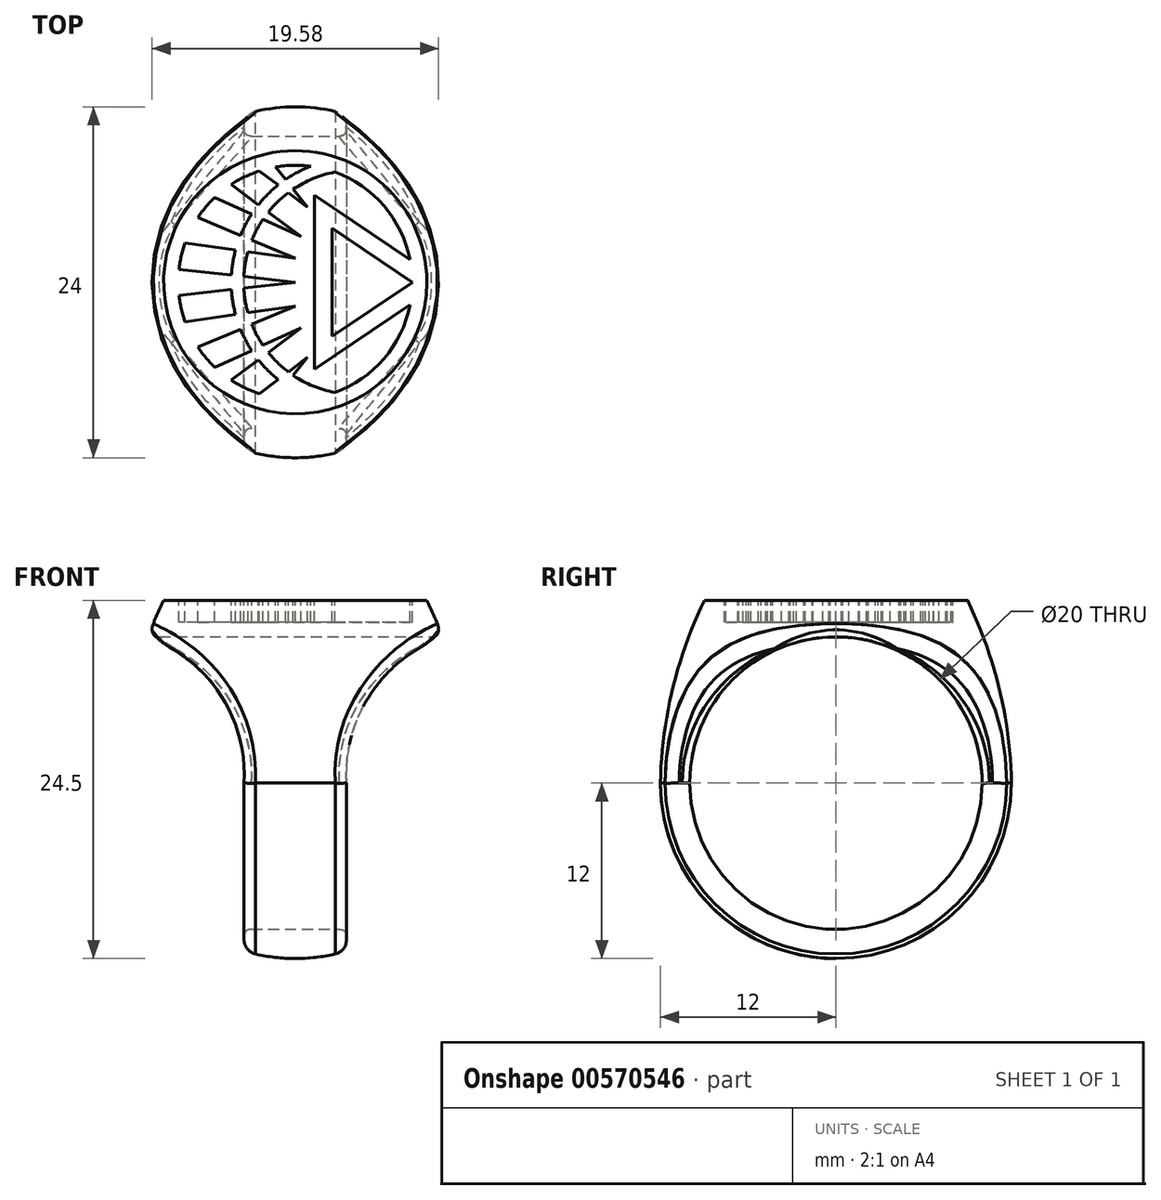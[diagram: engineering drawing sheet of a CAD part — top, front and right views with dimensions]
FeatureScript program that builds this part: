
annotation { "Feature Type Name" : "Feature", "Feature Type Description" : "" }
export const myFeature = defineFeature(function(context is Context, id is Id, definition is map)
    precondition{}
    {
        {
            var Q0;
            Q0=qCreatedBy(makeId("Right.planeOp"),FACE);
            var sketch = newSketch(context, id + "F0", { "sketchPlane" : qUnion([Q0])});
            skLineSegment(sketch, "E0", {"start": v(0, 0) * mm, "end": v(0, -24.5) * mm});
            skLineSegment(sketch, "E1", {"start": v(0, 0) * mm, "end": v(-9, 0) * mm});
            skArc(sketch, "E2", {"start": v(-12, -12.5) * mm, "mid": v(-8.49, -20.99) * mm, "end": v(0, -24.5) * mm});
            skLineSegment(sketch, "E3", {"start": v(0, -12.5) * mm, "end": v(-12, -12.5) * mm, "construction": true});
            skArc(sketch, "E4", {"start": v(-9, 0) * mm, "mid": v(-11.18, -6.09) * mm, "end": v(-12, -12.5) * mm});
            skSolve(sketch);
        }
        {
            var Q0;
            Q0=makeQuery(id+"F0.imprint","IMPRINT",FACE,{"disambiguationData":[TD([[makeQuery(id+"F0.imprint","IMPRINT",EDGE,{"derivedFrom":sQuery(id+"F0.wireOp",EDGE,"E0")}),-1.0]])]});
            var Q1;
            Q1=sQuery(id+"F0.wireOp",EDGE,"E0");
            revolve(context, id + "F1", {"entities" : qUnion([Q0]), "axis" : qUnion([Q1]), "revolveType" : RevolveType.FULL});
        }
        {
            var Q0;
            Q0=qCreatedBy(makeId("Right.planeOp"),FACE);
            var sketch = newSketch(context, id + "F2", { "sketchPlane" : qUnion([Q0])});
            skCircle(sketch, "E5", {"center": v(0, -12.5) * mm, "radius": 10 * mm});
            skSolve(sketch);
        }
        {
            var Q0;
            Q0=qSketchRegion(id+"F2",true);
            extrude(context, id + "F3", {"entities" : qUnion([Q0]), "operationType" : NewBodyOperationType.REMOVE, "oppositeDirection" : true, "depth" : 25 * mm, "offsetDistance" : 25 * mm, "symmetric" : true});
        }
        {
            var Q0;
            Q0=qCreatedBy(makeId("Front.planeOp"),FACE);
            var sketch = newSketch(context, id + "F4", { "sketchPlane" : qUnion([Q0])});
            skLineSegment(sketch, "E6", {"start": v(3.5, -26.5) * mm, "end": v(3.5, -12.5) * mm});
            skArc(sketch, "E7", {"start": v(10.15, -2.5) * mm, "mid": v(5.16, -6.39) * mm, "end": v(3.5, -12.5) * mm});
            skLineSegment(sketch, "E8", {"start": v(10.15, -2.5) * mm, "end": v(11.65, -2.5) * mm});
            skLineSegment(sketch, "E9", {"start": v(11.65, -2.5) * mm, "end": v(11.65, -26.5) * mm});
            skLineSegment(sketch, "E10", {"start": v(11.65, -26.5) * mm, "end": v(3.5, -26.5) * mm});
            skPoint(sketch, "E11.start.orphan", {"position": v(0, -24.5) * mm});
            skLineSegment(sketch, "E12", {"start": v(0, 0) * mm, "end": v(0, -24.5) * mm, "construction": true});
            skLineSegment(sketch, "E13.MirrorCS", {"start": v(-3.5, -26.5) * mm, "end": v(-3.5, -12.5) * mm});
            skArc(sketch, "E14.MirrorCS", {"start": v(-10.15, -2.5) * mm, "mid": v(-5.16, -6.39) * mm, "end": v(-3.5, -12.5) * mm});
            skLineSegment(sketch, "E15.MirrorCS", {"start": v(-11.65, -2.5) * mm, "end": v(-11.65, -26.5) * mm});
            skLineSegment(sketch, "E16.MirrorCS", {"start": v(-11.65, -26.5) * mm, "end": v(-3.5, -26.5) * mm});
            skLineSegment(sketch, "E17.MirrorCS", {"start": v(-10.15, -2.5) * mm, "end": v(-11.65, -2.5) * mm});
            skSolve(sketch);
        }
        {
            var Q0;
            Q0=qSketchRegion(id+"F4",true);
            extrude(context, id + "F5", {"entities" : qUnion([Q0]), "operationType" : NewBodyOperationType.REMOVE, "depth" : 25 * mm, "offsetDistance" : 25 * mm, "symmetric" : true});
        }
        {
            var Q0;
            Q0=makeQuery(id+"F1.opRevolve","SWEPT_FACE",FACE,{"disambiguationData":[OSD([sQuery(id+"F0.wireOp",EDGE,"E1")])]});
            var sketch = newSketch(context, id + "F6", { "sketchPlane" : qUnion([Q0])});
            skLineSegment(sketch, "E18", {"start": v(-8, 0) * mm, "end": v(8, 0) * mm, "construction": true});
            skArc(sketch, "E19", {"start": v(1.04, 7.93) * mm, "mid": v(-0.15, 8) * mm, "end": v(-1.34, 7.89) * mm});
            skLineSegment(sketch, "E20", {"start": v(7.85, 1.55) * mm, "end": v(1.3, 5.96) * mm});
            skLineSegment(sketch, "E21", {"start": v(1.3, 5.96) * mm, "end": v(1.3, 0) * mm});
            skLineSegment(sketch, "E22", {"start": v(8, 0) * mm, "end": v(2.5, 3.7) * mm});
            skLineSegment(sketch, "E23", {"start": v(2.5, 3.7) * mm, "end": v(2.5, 0) * mm});
            skLineSegment(sketch, "E24", {"start": v(0, 0) * mm, "end": v(-7.95, 0.89) * mm});
            skLineSegment(sketch, "E25", {"start": v(0.85, 5.13) * mm, "end": v(-0.14, 6.37) * mm});
            skLineSegment(sketch, "E26", {"start": v(0.85, 5.13) * mm, "end": v(-0.48, 6.13) * mm});
            skLineSegment(sketch, "E27", {"start": v(0.4, 3.12) * mm, "end": v(-1.85, 4.8) * mm});
            skLineSegment(sketch, "E28", {"start": v(0.4, 3.12) * mm, "end": v(-2.2, 4.3) * mm});
            skLineSegment(sketch, "E29", {"start": v(0, 1.63) * mm, "end": v(-2.97, 2.88) * mm});
            skLineSegment(sketch, "E30", {"start": v(0, 1.63) * mm, "end": v(-3.24, 2.09) * mm});
            skArc(sketch, "E31", {"start": v(2.7, 7.53) * mm, "mid": v(1.22, 7.1) * mm, "end": v(-0.14, 6.37) * mm});
            skArc(sketch, "E32", {"start": v(1.04, 7.93) * mm, "mid": v(0.16, 7.53) * mm, "end": v(-0.66, 7.03) * mm});
            skLineSegment(sketch, "E33.MirrorCS", {"start": v(8, 0) * mm, "end": v(2.5, -3.7) * mm});
            skLineSegment(sketch, "E34.MirrorCS", {"start": v(7.85, -1.55) * mm, "end": v(1.3, -5.96) * mm});
            skLineSegment(sketch, "E35.MirrorCS", {"start": v(2.5, -3.7) * mm, "end": v(2.5, 0) * mm});
            skLineSegment(sketch, "E36.MirrorCS", {"start": v(1.3, -5.96) * mm, "end": v(1.3, 0) * mm});
            skLineSegment(sketch, "E37.MirrorCS", {"start": v(0, 0) * mm, "end": v(-7.95, -0.89) * mm});
            skArc(sketch, "E38.MirrorCS", {"start": v(2.7, -7.53) * mm, "mid": v(1.22, -7.1) * mm, "end": v(-0.14, -6.37) * mm});
            skArc(sketch, "E39.MirrorCS", {"start": v(1.04, -7.93) * mm, "mid": v(0.16, -7.53) * mm, "end": v(-0.66, -7.03) * mm});
            skLineSegment(sketch, "E40.MirrorCS", {"start": v(0, -1.63) * mm, "end": v(-3.24, -2.09) * mm});
            skLineSegment(sketch, "E41.MirrorCS", {"start": v(0, -1.63) * mm, "end": v(-2.97, -2.88) * mm});
            skLineSegment(sketch, "E42.MirrorCS", {"start": v(0.4, -3.12) * mm, "end": v(-2.2, -4.3) * mm});
            skLineSegment(sketch, "E43.MirrorCS", {"start": v(0.4, -3.12) * mm, "end": v(-1.85, -4.8) * mm});
            skLineSegment(sketch, "E44.MirrorCS", {"start": v(0.85, -5.13) * mm, "end": v(-0.48, -6.13) * mm});
            skLineSegment(sketch, "E45.MirrorCS", {"start": v(0.85, -5.13) * mm, "end": v(-0.14, -6.37) * mm});
            skArc(sketch, "E46.trimOffspring", {"start": v(-1.17, 6.65) * mm, "mid": v(-1.89, 6.02) * mm, "end": v(-2.53, 5.3) * mm});
            skLineSegment(sketch, "E47.trimOffspring", {"start": v(-0.66, 7.03) * mm, "end": v(-1.34, 7.89) * mm});
            skLineSegment(sketch, "E48.trimOffspring", {"start": v(-1.17, 6.65) * mm, "end": v(-2.45, 7.62) * mm});
            skArc(sketch, "E49.trimOffspring", {"start": v(-0.48, 6.13) * mm, "mid": v(-1.2, 5.5) * mm, "end": v(-1.85, 4.8) * mm});
            skArc(sketch, "E50.trimOffspring", {"start": v(7.85, 1.55) * mm, "mid": v(6.06, 5.22) * mm, "end": v(2.7, 7.53) * mm});
            skLineSegment(sketch, "E51.trimOffspring", {"start": v(-2.53, 5.3) * mm, "end": v(-4.39, 6.7) * mm});
            skArc(sketch, "E52.trimOffspring", {"start": v(-2.99, 4.66) * mm, "mid": v(-3.4, 3.95) * mm, "end": v(-3.75, 3.21) * mm});
            skArc(sketch, "E53.trimOffspring", {"start": v(-2.2, 4.3) * mm, "mid": v(-2.63, 3.61) * mm, "end": v(-2.97, 2.88) * mm});
            skLineSegment(sketch, "E54.trimOffspring", {"start": v(-2.99, 4.66) * mm, "end": v(-5.5, 5.8) * mm});
            skArc(sketch, "E55.trimOffspring", {"start": v(-2.45, 7.62) * mm, "mid": v(-3.45, 7.22) * mm, "end": v(-4.39, 6.7) * mm});
            skArc(sketch, "E56.trimOffspring", {"start": v(-5.5, 5.8) * mm, "mid": v(-6.12, 5.16) * mm, "end": v(-6.66, 4.44) * mm});
            skArc(sketch, "E57.trimOffspring", {"start": v(-3.24, 2.09) * mm, "mid": v(-3.46, 1.05) * mm, "end": v(-3.53, 0) * mm});
            skLineSegment(sketch, "E58.trimOffspring", {"start": v(-3.75, 3.21) * mm, "end": v(-6.66, 4.44) * mm});
            skArc(sketch, "E59.trimOffspring", {"start": v(-4.08, 2.2) * mm, "mid": v(-4.3, 1.11) * mm, "end": v(-4.38, 0) * mm});
            skLineSegment(sketch, "E60.trimOffspring", {"start": v(-4.08, 2.2) * mm, "end": v(-7.53, 2.7) * mm});
            skArc(sketch, "E61.trimOffspring", {"start": v(-7.53, 2.7) * mm, "mid": v(-7.8, 1.8) * mm, "end": v(-7.95, 0.89) * mm});
            skArc(sketch, "E62.trimOffspring", {"start": v(-7.95, -0.89) * mm, "mid": v(-7.8, -1.8) * mm, "end": v(-7.53, -2.7) * mm});
            skArc(sketch, "E63.trimOffspring", {"start": v(-6.66, -4.44) * mm, "mid": v(-6.12, -5.16) * mm, "end": v(-5.5, -5.8) * mm});
            skArc(sketch, "E64.trimOffspring", {"start": v(-4.39, -6.7) * mm, "mid": v(-3.45, -7.22) * mm, "end": v(-2.45, -7.62) * mm});
            skArc(sketch, "E65.trimOffspring", {"start": v(-1.34, -7.89) * mm, "mid": v(-0.15, -8) * mm, "end": v(1.04, -7.93) * mm});
            skArc(sketch, "E66.trimOffspring", {"start": v(2.7, -7.53) * mm, "mid": v(6.06, -5.22) * mm, "end": v(7.85, -1.55) * mm});
            skLineSegment(sketch, "E67.trimOffspring", {"start": v(-0.66, -7.03) * mm, "end": v(-1.34, -7.89) * mm});
            skArc(sketch, "E68.trimOffspring", {"start": v(-1.17, -6.65) * mm, "mid": v(-1.89, -6.02) * mm, "end": v(-2.53, -5.3) * mm});
            skLineSegment(sketch, "E69.trimOffspring", {"start": v(-1.17, -6.65) * mm, "end": v(-2.45, -7.62) * mm});
            skArc(sketch, "E70.trimOffspring", {"start": v(-0.48, -6.13) * mm, "mid": v(-1.2, -5.5) * mm, "end": v(-1.85, -4.8) * mm});
            skLineSegment(sketch, "E71.trimOffspring", {"start": v(-2.53, -5.3) * mm, "end": v(-4.39, -6.7) * mm});
            skArc(sketch, "E72.trimOffspring", {"start": v(-2.2, -4.3) * mm, "mid": v(-2.63, -3.61) * mm, "end": v(-2.97, -2.88) * mm});
            skLineSegment(sketch, "E73.trimOffspring", {"start": v(-2.99, -4.66) * mm, "end": v(-5.5, -5.8) * mm});
            skArc(sketch, "E74.trimOffspring", {"start": v(-2.99, -4.66) * mm, "mid": v(-3.4, -3.95) * mm, "end": v(-3.75, -3.21) * mm});
            skLineSegment(sketch, "E75.trimOffspring", {"start": v(-3.75, -3.21) * mm, "end": v(-6.66, -4.44) * mm});
            skArc(sketch, "E76.trimOffspring", {"start": v(-3.24, -2.09) * mm, "mid": v(-3.46, -1.05) * mm, "end": v(-3.53, 0) * mm});
            skLineSegment(sketch, "E77.trimOffspring", {"start": v(-4.08, -2.2) * mm, "end": v(-7.53, -2.7) * mm});
            skArc(sketch, "E78.trimOffspring", {"start": v(-4.08, -2.2) * mm, "mid": v(-4.3, -1.11) * mm, "end": v(-4.38, 0) * mm});
            skSolve(sketch);
        }
        {
            var Q0;
            {var subQ4=sQuery(id+"F6.wireOp",EDGE,"E60.trimOffspring");Q0=makeQuery(id+"F6.imprint","IMPRINT",FACE,{"disambiguationData":[TD([[makeQuery(id+"F6.imprint","IMPRINT",EDGE,{"derivedFrom":subQ4}),1.0]])]});}
            var Q1;
            Q1=makeQuery(id+"F6.imprint","IMPRINT",FACE,{"disambiguationData":[TD([[makeQuery(id+"F6.imprint","IMPRINT",EDGE,{"derivedFrom":sQuery(id+"F6.wireOp",EDGE,"E52.trimOffspring")}),-1.0]])]});
            var Q2;
            Q2=makeQuery(id+"F6.imprint","IMPRINT",FACE,{"disambiguationData":[TD([[makeQuery(id+"F6.imprint","IMPRINT",EDGE,{"derivedFrom":sQuery(id+"F6.wireOp",EDGE,"E46.trimOffspring")}),-1.0]])]});
            var Q3;
            Q3=makeQuery(id+"F6.imprint","IMPRINT",FACE,{"disambiguationData":[TD([[makeQuery(id+"F6.imprint","IMPRINT",EDGE,{"derivedFrom":sQuery(id+"F6.wireOp",EDGE,"E19")}),1.0]])]});
            var Q4;
            Q4=makeQuery(id+"F6.imprint","IMPRINT",FACE,{"disambiguationData":[TD([[makeQuery(id+"F6.imprint","IMPRINT",EDGE,{"derivedFrom":sQuery(id+"F6.wireOp",EDGE,"E20")}),-1.0]])]});
            var Q5;
            Q5=makeQuery(id+"F6.imprint","IMPRINT",FACE,{"disambiguationData":[TD([[makeQuery(id+"F6.imprint","IMPRINT",EDGE,{"derivedFrom":sQuery(id+"F6.wireOp",EDGE,"E22")}),1.0]])]});
            var Q6;
            {var subQ0=sQuery(id+"F6.wireOp",EDGE,"E62.trimOffspring");Q6=makeQuery(id+"F6.imprint","IMPRINT",FACE,{"disambiguationData":[TD([[makeQuery(id+"F6.imprint","IMPRINT",EDGE,{"derivedFrom":subQ0}),1.0]])]});}
            var Q7;
            Q7=makeQuery(id+"F6.imprint","IMPRINT",FACE,{"disambiguationData":[TD([[makeQuery(id+"F6.imprint","IMPRINT",EDGE,{"derivedFrom":sQuery(id+"F6.wireOp",EDGE,"E63.trimOffspring")}),1.0]])]});
            var Q8;
            Q8=makeQuery(id+"F6.imprint","IMPRINT",FACE,{"disambiguationData":[TD([[makeQuery(id+"F6.imprint","IMPRINT",EDGE,{"derivedFrom":sQuery(id+"F6.wireOp",EDGE,"E64.trimOffspring")}),1.0]])]});
            var Q9;
            Q9=makeQuery(id+"F6.imprint","IMPRINT",FACE,{"disambiguationData":[TD([[makeQuery(id+"F6.imprint","IMPRINT",EDGE,{"derivedFrom":sQuery(id+"F6.wireOp",EDGE,"E39.MirrorCS")}),1.0]])]});
            extrude(context, id + "F7", {"entities" : qUnion([Q0, Q1, Q2, Q3, Q4, Q5, Q6, Q7, Q8, Q9]), "operationType" : NewBodyOperationType.REMOVE, "oppositeDirection" : true, "depth" : 1.5 * mm, "offsetDistance" : 25 * mm});
        }
        {
            var Q0;
            Q0=makeQuery(id+"F5.boolean.opBoolean","INTERSECT",EDGE,{"disambiguationData":[OD(1.0)],"derivedFrom":[makeQuery(id+"F1.opRevolve","SWEPT_FACE",FACE,{"disambiguationData":[OSD([sQuery(id+"F0.wireOp",EDGE,"E4")])]}),makeQuery(id+"F5.opExtrude","SWEPT_FACE",FACE,{"disambiguationData":[OSD([sQuery(id+"F4.wireOp",EDGE,"E14.MirrorCS")])]})]});
            var Q1;
            Q1=makeQuery(id+"F5.boolean.opBoolean","INTERSECT",EDGE,{"derivedFrom":[makeQuery(id+"F1.opRevolve","SWEPT_FACE",FACE,{"disambiguationData":[OSD([sQuery(id+"F0.wireOp",EDGE,"E2")])]}),makeQuery(id+"F5.opExtrude","SWEPT_FACE",FACE,{"disambiguationData":[OSD([sQuery(id+"F4.wireOp",EDGE,"E13.MirrorCS")])]})]});
            var Q2;
            Q2=makeQuery(id+"F5.boolean.opBoolean","INTERSECT",EDGE,{"disambiguationData":[OD(1.0)],"derivedFrom":[makeQuery(id+"F1.opRevolve","SWEPT_FACE",FACE,{"disambiguationData":[OSD([sQuery(id+"F0.wireOp",EDGE,"E4")])]}),makeQuery(id+"F5.opExtrude","SWEPT_FACE",FACE,{"disambiguationData":[OSD([sQuery(id+"F4.wireOp",EDGE,"E7")])]})]});
            var Q3;
            Q3=makeQuery(id+"F5.boolean.opBoolean","INTERSECT",EDGE,{"derivedFrom":[makeQuery(id+"F1.opRevolve","SWEPT_FACE",FACE,{"disambiguationData":[OSD([sQuery(id+"F0.wireOp",EDGE,"E2")])]}),makeQuery(id+"F5.opExtrude","SWEPT_FACE",FACE,{"disambiguationData":[OSD([sQuery(id+"F4.wireOp",EDGE,"E6")])]})]});
            fillet(context, id + "F8", {"entities" : qUnion([Q0, Q1, Q2, Q3]), "radius" : 1 * mm, "allowEdgeOverflow" : false});
        }
        {
            var Q0;
            Q0=makeQuery(id+"F5.boolean.opBoolean","INTERSECT",EDGE,{"disambiguationData":[OD(1.0)],"derivedFrom":[makeQuery(id+"F3.boolean.opBoolean","COPY",FACE,{"derivedFrom":makeQuery(id+"F3.opExtrude","SWEPT_FACE",FACE,{"disambiguationData":[OSD([sQuery(id+"F2.wireOp",EDGE,"E5")])]})}),makeQuery(id+"F5.opExtrude","SWEPT_FACE",FACE,{"disambiguationData":[OSD([sQuery(id+"F4.wireOp",EDGE,"E14.MirrorCS")])]})]});
            var Q1;
            Q1=makeQuery(id+"F5.boolean.opBoolean","INTERSECT",EDGE,{"derivedFrom":[makeQuery(id+"F3.boolean.opBoolean","COPY",FACE,{"derivedFrom":makeQuery(id+"F3.opExtrude","SWEPT_FACE",FACE,{"disambiguationData":[OSD([sQuery(id+"F2.wireOp",EDGE,"E5")])]})}),makeQuery(id+"F5.opExtrude","SWEPT_FACE",FACE,{"disambiguationData":[OSD([sQuery(id+"F4.wireOp",EDGE,"E13.MirrorCS")])]})]});
            var Q2;
            Q2=makeQuery(id+"F5.boolean.opBoolean","INTERSECT",EDGE,{"disambiguationData":[OD(0.0)],"derivedFrom":[makeQuery(id+"F3.boolean.opBoolean","COPY",FACE,{"derivedFrom":makeQuery(id+"F3.opExtrude","SWEPT_FACE",FACE,{"disambiguationData":[OSD([sQuery(id+"F2.wireOp",EDGE,"E5")])]})}),makeQuery(id+"F5.opExtrude","SWEPT_FACE",FACE,{"disambiguationData":[OSD([sQuery(id+"F4.wireOp",EDGE,"E14.MirrorCS")])]})]});
            var Q3;
            Q3=makeQuery(id+"F5.boolean.opBoolean","INTERSECT",EDGE,{"disambiguationData":[OD(0.0)],"derivedFrom":[makeQuery(id+"F3.boolean.opBoolean","COPY",FACE,{"derivedFrom":makeQuery(id+"F3.opExtrude","SWEPT_FACE",FACE,{"disambiguationData":[OSD([sQuery(id+"F2.wireOp",EDGE,"E5")])]})}),makeQuery(id+"F5.opExtrude","SWEPT_FACE",FACE,{"disambiguationData":[OSD([sQuery(id+"F4.wireOp",EDGE,"E7")])]})]});
            var Q4;
            Q4=makeQuery(id+"F3.boolean.opBoolean","COPY",FACE,{"derivedFrom":makeQuery(id+"F3.opExtrude","SWEPT_FACE",FACE,{"disambiguationData":[OSD([sQuery(id+"F2.wireOp",EDGE,"E5")])]})});
            fillet(context, id + "F9", {"entities" : qUnion([Q0, Q1, Q2, Q3, Q4]), "radius" : .5 * mm, "rho" : 0.5, "crossSection" : FilletCrossSection.CONIC, "allowEdgeOverflow" : false});
        }
    });
